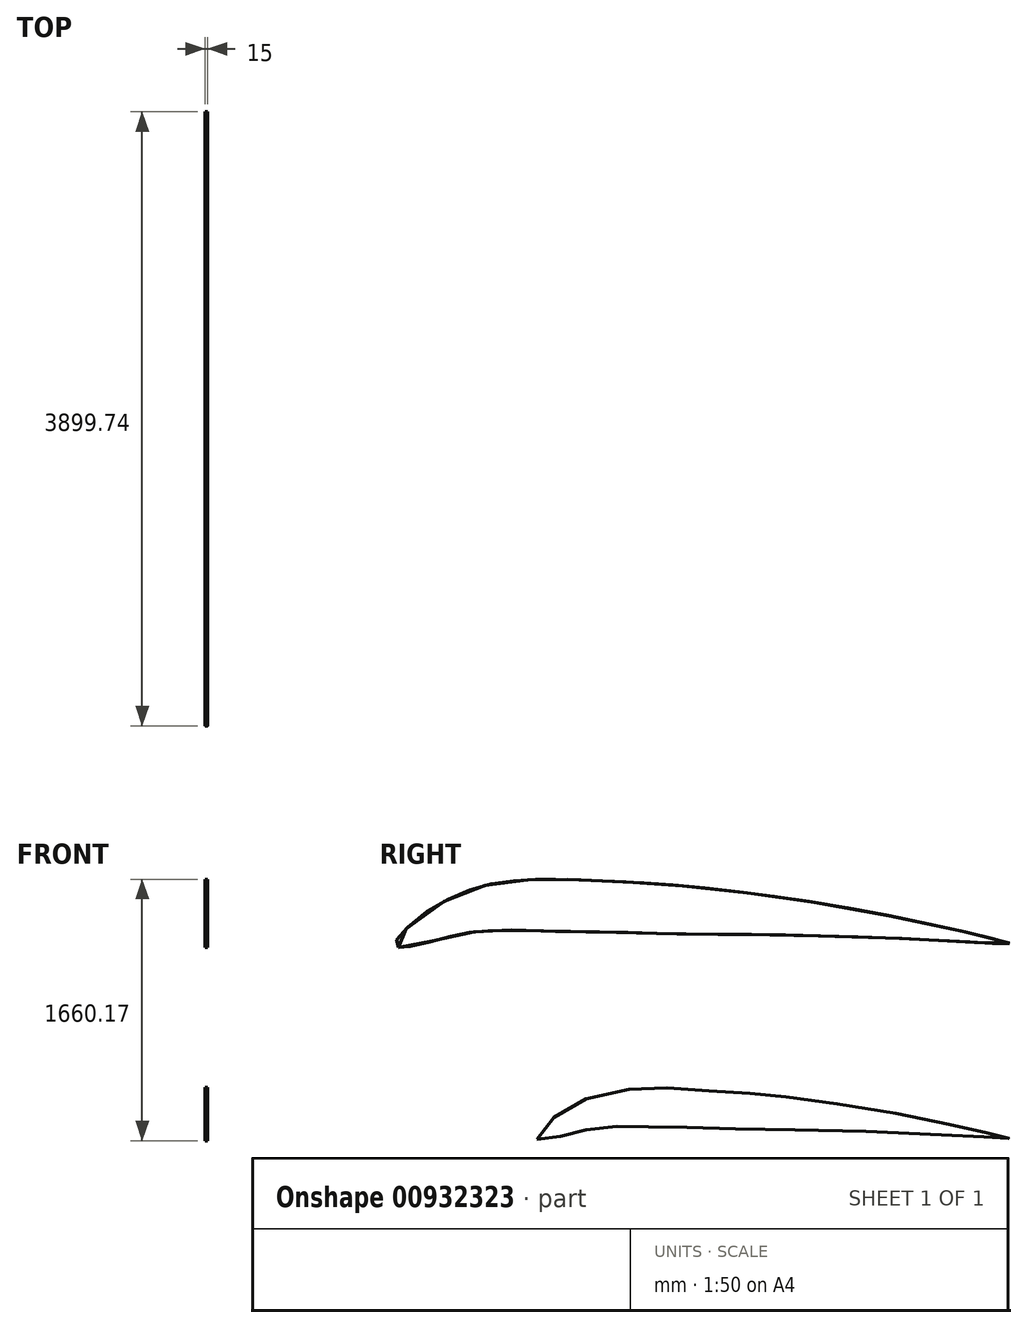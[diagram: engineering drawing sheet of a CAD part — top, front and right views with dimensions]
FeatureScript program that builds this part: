
annotation { "Feature Type Name" : "Feature", "Feature Type Description" : "" }
export const myFeature = defineFeature(function(context is Context, id is Id, definition is map)
    precondition{}
    {
        {
            var Q0;
            Q0=qCreatedBy(makeId("Right.planeOp"),FACE);
            var sketch = newSketch(context, id + "F0", { "sketchPlane" : qUnion([Q0])});
            skFitSpline(sketch, "E0", {"points": [v(-1017.58, -152.45) * mm, v(-978.14, -74.97) * mm, v(-815.11, 47.22) * mm, v(-602.3, 136.1) * mm, v(-287.6, 176) * mm, v(-120.53, 169.38) * mm, v(219.42, 147.48) * mm, v(399.88, 135.24) * mm, v(656.16, 106.12) * mm, v(1160.81, 29.8) * mm, v(1624.96, -62.8) * mm, v(1842.41, -113.27) * mm, v(1896.77, -126.86) * mm, v(1982.37, -146.18) * mm, v(1866.46, -138.35) * mm, v(1758.12, -133.49) * mm, v(1058.05, -101.62) * mm, v(361.05, -88.03) * mm, v(-42.78, -78.33) * mm, v(-287.6, -75.43) * mm, v(-444.67, -72.18) * mm, v(-594.17, -74.44) * mm, v(-739.78, -101.62) * mm, v(-840.05, -124.65) * mm, v(-958.79, -157.56) * mm, v(-1017.58, -152.45) * mm]});
            skLineSegment(sketch, "E1", {"start": v(-1017.58, -152.45) * mm, "end": v(1982.37, -169.3) * mm, "construction": true});
            skLineSegment(sketch, "E2", {"start": v(-287.6, 59.5) * mm, "end": v(-287.6, 176) * mm, "construction": true});
            skLineSegment(sketch, "E3", {"start": v(-287.6, 59.5) * mm, "end": v(-1017.58, 63.6) * mm, "construction": true});
            skLineSegment(sketch, "E4", {"start": v(-1017.58, 421.17) * mm, "end": v(1982.37, 404.32) * mm, "construction": true});
            skSolve(sketch);
        }
        {
            var Q0;
            Q0=makeQuery(id+"F0.imprint","IMPRINT",FACE,{"disambiguationData":[TD([[makeQuery(id+"F0.imprint","IMPRINT",EDGE,{"derivedFrom":sQuery(id+"F0.wireOp",EDGE,"E0")}),-1.0]])]});
            extrude(context, id + "F1", {"entities" : qUnion([Q0]), "depth" : 15 * mm, "offsetDistance" : 25 * mm});
        }
        {
            var Q0;
            Q0=qCreatedBy(makeId("Right.planeOp"),FACE);
            var sketch = newSketch(context, id + "F2", { "sketchPlane" : qUnion([Q0])});
            skLineSegment(sketch, "E5", {"start": v(-2004.64, 1808.43) * mm, "end": v(1995.36, 1808.43) * mm, "construction": true});
            skFitSpline(sketch, "E6", {"points": [v(-1895.49, 1067.04) * mm, v(-1913.21, 1074.64) * mm, v(-1910.68, 1106.3) * mm, v(-1871.43, 1160.74) * mm, v(-1725.82, 1286.1) * mm, v(-1558.68, 1383.6) * mm, v(-1386.48, 1448.17) * mm, v(-1233.27, 1481.09) * mm, v(-1057.27, 1496.28) * mm, v(-933.18, 1498.81) * mm, v(-723, 1493.75) * mm, v(-386.2, 1477.29) * mm, v(-100.03, 1457.03) * mm, v(281.09, 1416.51) * mm, v(691.33, 1360.8) * mm, v(1209.2, 1269.63) * mm, v(1710.61, 1162) * mm, v(1943.6, 1103.76) * mm, v(1984.11, 1091.1) * mm, v(1892.95, 1091.1) * mm, v(1656.17, 1105.03) * mm, v(1030.67, 1132.89) * mm, v(498.87, 1145.55) * mm, v(34.18, 1150.61) * mm, v(-333.01, 1158.21) * mm, v(-663.49, 1165.8) * mm, v(-981.3, 1170.87) * mm, v(-1143.37, 1175.94) * mm, v(-1264.92, 1173.4) * mm, v(-1400.4, 1165.8) * mm, v(-1548.55, 1140.48) * mm, v(-1723.28, 1094.9) * mm, v(-1862.56, 1067.04) * mm, v(-1895.49, 1067.04) * mm]});
            skSolve(sketch);
        }
        {
            var Q0;
            Q0=makeQuery(id+"F2.imprint","IMPRINT",FACE,{"disambiguationData":[TD([[makeQuery(id+"F2.imprint","IMPRINT",EDGE,{"derivedFrom":sQuery(id+"F2.wireOp",EDGE,"E6")}),-1.0]])]});
            extrude(context, id + "F3", {"entities" : qUnion([Q0]), "depth" : 15 * mm, "offsetDistance" : 25 * mm});
        }
    });
